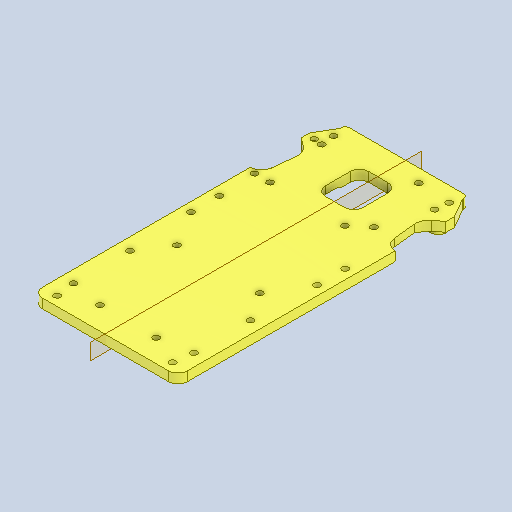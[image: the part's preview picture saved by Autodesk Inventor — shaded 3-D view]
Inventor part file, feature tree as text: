
AUTODESK INVENTOR PART (.ipt)
format: ipt  version: 2022.6 (Build 266554000, 554)  size: 404,480 bytes
history: native  units: mm
features: sketch x13, extrude x7, hole x6, fillet x4, projected_geometry x4, other x3, mirror x1, reference x1
ambient origin geometry x8: Origin, YZ Plane, XZ Plane, XY Plane, X Axis, Y Axis, Z Axis, Center Point
bodies: Solid1 (feature_tree)
feature tree (39):
  extrude  "Extrusion1"  Depth=77.0mm
  fillet  "Fillet1"  Radius=5.0mm
  hole  "Bearing + Motor"  [1 undecoded]
  hole  "Front US"  [1 undecoded]
  hole  "Brass stands"  [1 undecoded]
  hole  "Steering"  [1 undecoded]
  hole  "Side US"  [1 undecoded]
  extrude  "Extrusion3"  Depth=2.0mm
  extrude  "Extrusion5"  Depth=2.0mm
  mirror  "Mirror2"
  fillet  "Fillet4"  Radius=38.0mm
  hole  "Servo Mount"  [1 undecoded]
  extrude  "Extrusion6"  Depth=2.0mm
  fillet  "Fillet6"  Radius=12.0mm
  extrude  "Extrusion7"  Depth=2.0mm
  extrude  "Extrusion8"  Depth=10.0mm TaperAngle=0.0deg
  extrude  "Extrusion9"  Depth=2.0mm
  fillet  "Fillet7"  Radius=2.0mm
  sketch  "Sketch1"  dims[d0=160.0mm d1=77.0mm d2=5.0mm d3=0.0mm]
  sketch  "Sketch2"  dims[d4=5.0mm]
  projected_geometry  "Projected Loop1"
  sketch  "Sketch5"  dims[d9=3.4mm d10=6.0mm d11=4.0mm d12=2.0mm d13=90.0deg d14=8.0mm d15=20.594885mm d16=15.0mm]
  sketch  "Sketch6"  dims[d17=64.0mm d50=12.0mm]
  sketch  "Sketch7"  dims[d51=30.0mm]
  projected_geometry  "Projected Loop3"
  sketch  "Sketch8"  dims[d52=3.4mm d53=6.0mm d54=4.0mm d55=2.0mm d56=90.0deg d57=8.0mm d58=20.594885mm d60=61.5mm]
  sketch  "Sketch9"  dims[d63=3.4mm d64=6.0mm d65=6.5mm d66=1.3mm d67=90.0deg d68=8.0mm d69=20.594885mm d71=8.0mm]
  projected_geometry  "Projected Loop4"
  sketch  "Sketch11"  dims[d72=5.0mm d74=60.0mm]
  reference  "Reference1"
  sketch  "Sketch13"  dims[d76=3.4mm d77=6.0mm d78=4.0mm d79=2.0mm d80=90.0deg d81=8.0mm d82=20.594885mm d83=5.0mm]
  projected_geometry  "Projected Loop13"
  sketch  "Sketch14"  dims[d84=15.0mm]
  sketch  "Sketch15"  dims[d85=3.4mm d86=6.0mm d87=4.0mm d88=2.0mm d89=90.0deg d90=8.0mm d91=20.594885mm d93=1.0mm d94=38.0mm]
  sketch  "Sketch16"  dims[d95=20.0mm d96=28.5mm]
  sketch  "Sketch17"  dims[d97=10.0mm d98=0.0mm d114=14.5mm d115=12.0mm d116=12.0mm d118=10.0mm d119=0.0mm d129=9.0mm d140=2.0mm d145=4.0mm d146=3.4mm d147=6.0mm d148=4.0mm d149=2.0mm d150=90.0deg d151=10.0mm d152=20.594885mm d156=3.2mm d157=4.0mm d158=14.6mm d159=1.8mm d160=0.0mm d161=16.45mm d165=12.25mm d167=8.5mm d168=32.2mm d169=7.1mm d170=7.0mm d171=90.0deg d172=30.0mm d173=15.0mm d174=10.0mm d178=15.0mm d179=5.0mm d180=26.5mm d181=2.6mm d182=20.0mm d183=35.0mm d184=1.0mm d185=0.0mm d187=2.0mm d188=8.0mm d189=2.75mm d190=0.0mm d191=6.0mm d192=12.0mm d193=10.0mm d194=0.0mm d195=2.0mm]
  other  "<userpath>\Desktop\WRO\vehicle v4.6.2\WRO FE vehicle v4.1.iam"
  other  "WRO FE vehicle v4.1.iam"
  other  "Battery Mount V2:1"
note: 6 required parameter values undecoded (feature->parameter linkage not recoverable at this tier; creation-order binding heuristic only, values carry confidence <= 0.55)
